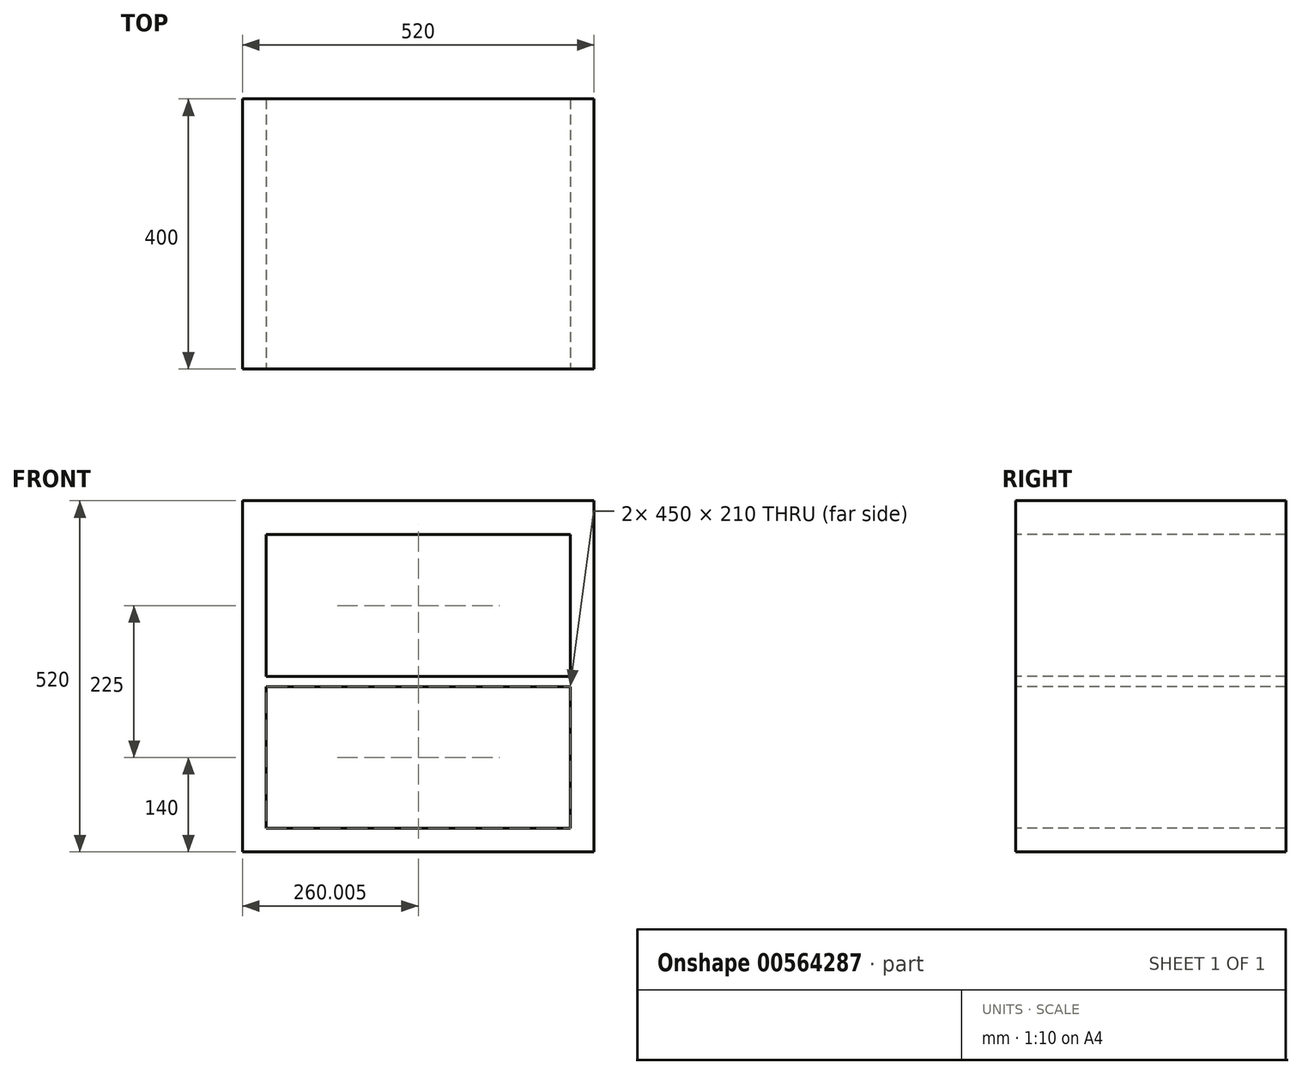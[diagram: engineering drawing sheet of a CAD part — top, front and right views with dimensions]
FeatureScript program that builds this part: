
annotation { "Feature Type Name" : "Feature", "Feature Type Description" : "" }
export const myFeature = defineFeature(function(context is Context, id is Id, definition is map)
    precondition{}
    {
        {
            var Q0;
            Q0=qCreatedBy(makeId("Top.planeOp"),FACE);
            var sketch = newSketch(context, id + "F0", { "sketchPlane" : qUnion([Q0])});
            skLineSegment(sketch, "E0.bottom", {"start": v(-252.99, 107.03) * mm, "end": v(267.01, 107.03) * mm});
            skLineSegment(sketch, "E0.top", {"start": v(-252.99, -292.97) * mm, "end": v(267.01, -292.97) * mm});
            skLineSegment(sketch, "E0.left", {"start": v(-252.99, 107.03) * mm, "end": v(-252.99, -292.97) * mm});
            skLineSegment(sketch, "E0.right", {"start": v(267.01, 107.03) * mm, "end": v(267.01, -292.97) * mm});
            skSolve(sketch);
        }
        {
            var Q0;
            Q0=makeQuery(id+"F0.imprint","IMPRINT",FACE,{"disambiguationData":[TD([[makeQuery(id+"F0.imprint","IMPRINT",EDGE,{"derivedFrom":sQuery(id+"F0.wireOp",EDGE,"E0.bottom")}),-1.0]])]});
            extrude(context, id + "F1", {"entities" : qUnion([Q0]), "depth" : 520 * mm, "offsetDistance" : 25 * mm});
        }
        {
            var Q0;
            Q0=makeQuery(id+"F1.opExtrude","SWEPT_FACE",FACE,{"disambiguationData":[OSD([sQuery(id+"F0.wireOp",EDGE,"E0.top")])]});
            var sketch = newSketch(context, id + "F2", { "sketchPlane" : qUnion([Q0])});
            skLineSegment(sketch, "E1.bottom", {"start": v(232.01, 35) * mm, "end": v(-217.99, 35) * mm});
            skLineSegment(sketch, "E1.top", {"start": v(232.01, 245) * mm, "end": v(-217.99, 245) * mm});
            skLineSegment(sketch, "E1.left", {"start": v(232.01, 35) * mm, "end": v(232.01, 245) * mm});
            skLineSegment(sketch, "E1.right", {"start": v(-217.99, 35) * mm, "end": v(-217.99, 245) * mm});
            skLineSegment(sketch, "E2.bottom", {"start": v(232.01, 260) * mm, "end": v(-217.99, 260) * mm});
            skLineSegment(sketch, "E2.top", {"start": v(232.01, 470) * mm, "end": v(-217.99, 470) * mm});
            skLineSegment(sketch, "E2.left", {"start": v(232.01, 260) * mm, "end": v(232.01, 470) * mm});
            skLineSegment(sketch, "E2.right", {"start": v(-217.99, 260) * mm, "end": v(-217.99, 470) * mm});
            skSolve(sketch);
        }
        {
            var Q0;
            Q0=makeQuery(id+"F2.imprint","IMPRINT",FACE,{"disambiguationData":[TD([[makeQuery(id+"F2.imprint","IMPRINT",EDGE,{"derivedFrom":sQuery(id+"F2.wireOp",EDGE,"E1.bottom")}),-1.0]])]});
            var Q1;
            Q1=makeQuery(id+"F2.imprint","IMPRINT",FACE,{"disambiguationData":[TD([[makeQuery(id+"F2.imprint","IMPRINT",EDGE,{"derivedFrom":sQuery(id+"F2.wireOp",EDGE,"E2.bottom")}),-1.0]])]});
            extrude(context, id + "F3", {"entities" : qUnion([Q0, Q1]), "operationType" : NewBodyOperationType.REMOVE, "endBound" : BoundingType.THROUGH_ALL, "oppositeDirection" : true, "depth" : 25 * mm, "offsetDistance" : 25 * mm});
        }
    });
